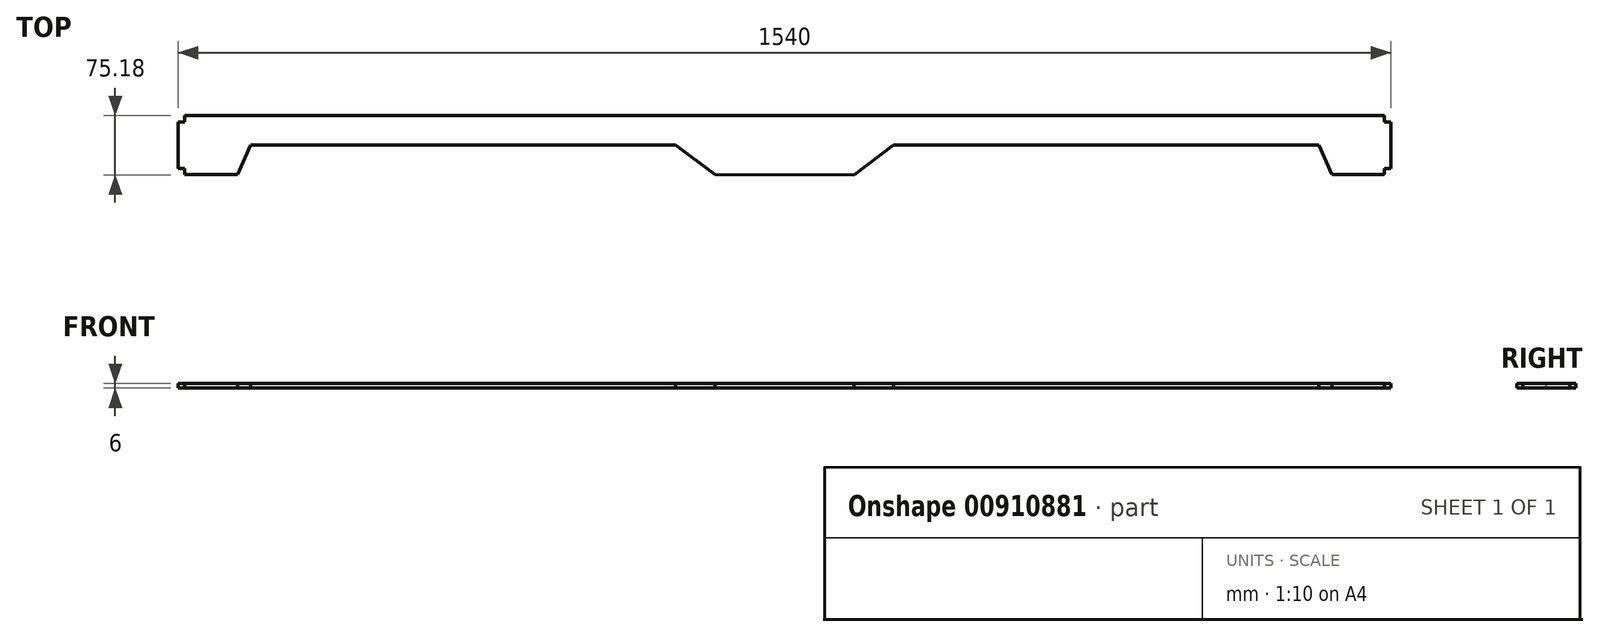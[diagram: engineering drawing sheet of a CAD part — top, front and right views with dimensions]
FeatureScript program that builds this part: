
annotation { "Feature Type Name" : "Feature", "Feature Type Description" : "" }
export const myFeature = defineFeature(function(context is Context, id is Id, definition is map)
    precondition{}
    {
        {
            var Q0;
            Q0=qCreatedBy(makeId("Top.planeOp"),FACE);
            var sketch = newSketch(context, id + "F0", { "sketchPlane" : qUnion([Q0])});
            skLineSegment(sketch, "E0", {"start": v(-679.66, 201) * mm, "end": v(860.34, 201) * mm});
            skLineSegment(sketch, "E1", {"start": v(90.34, 346.1) * mm, "end": v(90.34, 108.39) * mm, "construction": true});
            skPoint(sketch, "E1.startSnap0", {"position": v(90.34, 201) * mm});
            skLineSegment(sketch, "E2", {"start": v(-679.66, 201) * mm, "end": v(-679.66, 126) * mm});
            skLineSegment(sketch, "E3", {"start": v(-679.66, 126) * mm, "end": v(-604.66, 126) * mm});
            skLineSegment(sketch, "E4", {"start": v(-604.66, 126) * mm, "end": v(-588.16, 163.5) * mm});
            skPoint(sketch, "E4.endSnap0", {"position": v(-679.66, 163.5) * mm});
            skLineSegment(sketch, "E5", {"start": v(860.34, 201) * mm, "end": v(860.34, 126) * mm});
            skLineSegment(sketch, "E6", {"start": v(860.34, 126) * mm, "end": v(785.34, 126) * mm});
            skLineSegment(sketch, "E7", {"start": v(-48.16, 288.48) * mm, "end": v(-48.16, 99.05) * mm, "construction": true});
            skLineSegment(sketch, "E8", {"start": v(228.84, 290.8) * mm, "end": v(228.84, 101.08) * mm, "construction": true});
            skLineSegment(sketch, "E9", {"start": v(1.84, 286.74) * mm, "end": v(1.84, 99.73) * mm, "construction": true});
            skLineSegment(sketch, "E10", {"start": v(178.84, 290.8) * mm, "end": v(178.84, 102.44) * mm, "construction": true});
            skLineSegment(sketch, "E11", {"start": v(-588.16, 163.5) * mm, "end": v(-48.16, 163.5) * mm});
            skLineSegment(sketch, "E12", {"start": v(-48.16, 163.5) * mm, "end": v(1.84, 126) * mm});
            skLineSegment(sketch, "E13", {"start": v(1.84, 126) * mm, "end": v(178.84, 125.82) * mm});
            skLineSegment(sketch, "E14", {"start": v(178.84, 125.82) * mm, "end": v(228.84, 163.5) * mm});
            skPoint(sketch, "E14.endSnap0", {"position": v(228.84, 195.94) * mm});
            skLineSegment(sketch, "E15", {"start": v(228.84, 163.5) * mm, "end": v(768.84, 163.5) * mm});
            skLineSegment(sketch, "E16", {"start": v(768.84, 163.5) * mm, "end": v(785.34, 126) * mm});
            skSolve(sketch);
        }
        {
            var Q0;
            Q0 = qSketchRegion(id + "F0", true);
            extrude(context, id + "F1", {"entities" : qUnion([Q0]), "depth" : -6 * mm, "offsetDistance" : 25 * mm});
        }
        {
            var Q0;
            Q0=makeQuery(id+"F0.imprint","IMPRINT",FACE,{"disambiguationData":[TD([[makeQuery(id+"F0.imprint","IMPRINT",EDGE,{"derivedFrom":sQuery(id+"F0.wireOp",EDGE,"E0")}),-1.0]])]});
            var sketch = newSketch(context, id + "F2", { "sketchPlane" : qUnion([Q0])});
            skLineSegment(sketch, "E17.bottom", {"start": v(-679.72, 201.24) * mm, "end": v(-671.72, 201.24) * mm});
            skLineSegment(sketch, "E17.top", {"start": v(-679.72, 193.24) * mm, "end": v(-671.72, 193.24) * mm});
            skLineSegment(sketch, "E17.left", {"start": v(-679.72, 201.24) * mm, "end": v(-679.72, 193.24) * mm});
            skLineSegment(sketch, "E17.right", {"start": v(-671.72, 201.24) * mm, "end": v(-671.72, 193.24) * mm});
            skLineSegment(sketch, "E18.bottom", {"start": v(-679.74, 125.97) * mm, "end": v(-671.74, 125.97) * mm});
            skLineSegment(sketch, "E18.top", {"start": v(-679.74, 133.97) * mm, "end": v(-671.74, 133.97) * mm});
            skLineSegment(sketch, "E18.left", {"start": v(-679.74, 125.97) * mm, "end": v(-679.74, 133.97) * mm});
            skLineSegment(sketch, "E18.right", {"start": v(-671.74, 125.97) * mm, "end": v(-671.74, 133.97) * mm});
            skLineSegment(sketch, "E19.bottom", {"start": v(860.6, 201.11) * mm, "end": v(852.6, 201.11) * mm});
            skLineSegment(sketch, "E19.top", {"start": v(860.6, 193.11) * mm, "end": v(852.6, 193.11) * mm});
            skLineSegment(sketch, "E19.left", {"start": v(860.6, 201.11) * mm, "end": v(860.6, 193.11) * mm});
            skLineSegment(sketch, "E19.right", {"start": v(852.6, 201.11) * mm, "end": v(852.6, 193.11) * mm});
            skLineSegment(sketch, "E20.bottom", {"start": v(860.46, 125.93) * mm, "end": v(852.46, 125.93) * mm});
            skLineSegment(sketch, "E20.top", {"start": v(860.46, 133.93) * mm, "end": v(852.46, 133.93) * mm});
            skLineSegment(sketch, "E20.left", {"start": v(860.46, 125.93) * mm, "end": v(860.46, 133.93) * mm});
            skLineSegment(sketch, "E20.right", {"start": v(852.46, 125.93) * mm, "end": v(852.46, 133.93) * mm});
            skSolve(sketch);
        }
        {
            var Q0;
            Q0 = qSketchRegion(id + "F2", true);
            extrude(context, id + "F3", {"entities" : qUnion([Q0]), "operationType" : NewBodyOperationType.REMOVE, "oppositeDirection" : true, "depth" : 6.1 * mm, "offsetDistance" : 25 * mm});
        }
    });
